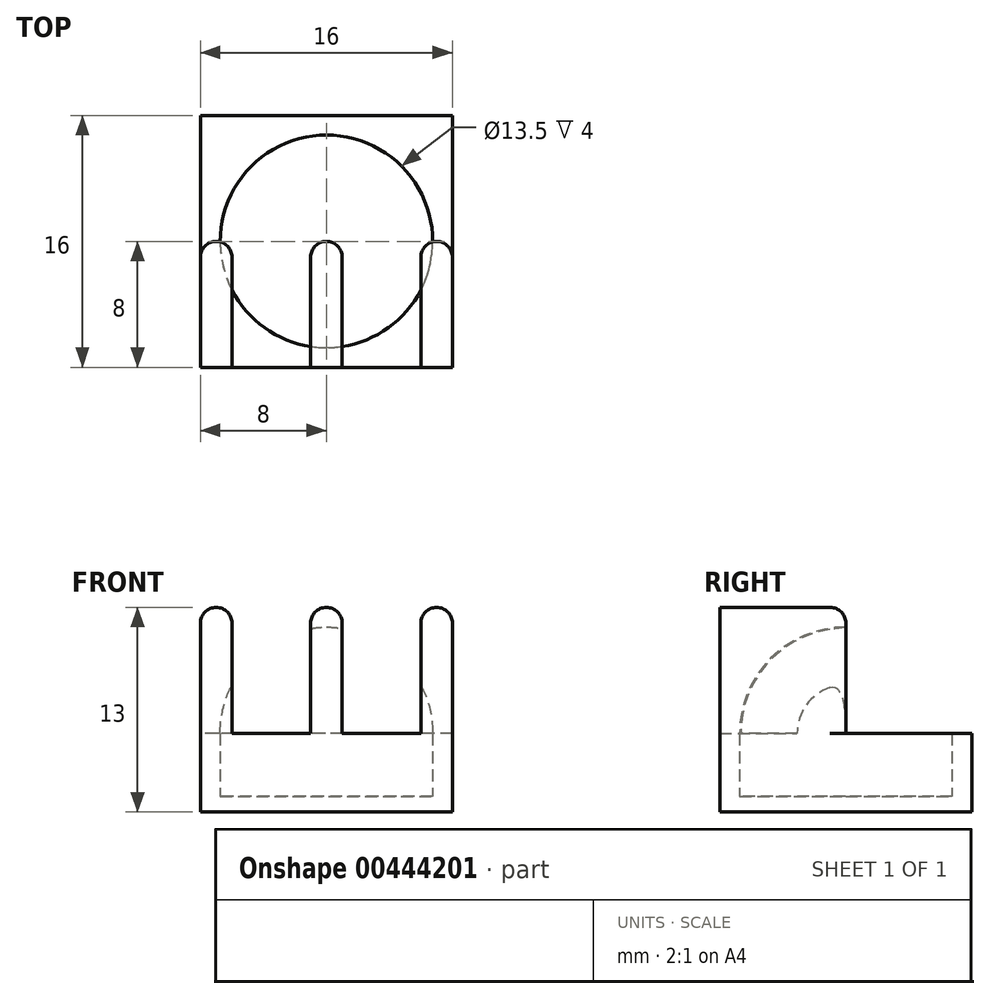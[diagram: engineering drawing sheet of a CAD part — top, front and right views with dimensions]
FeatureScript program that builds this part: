
annotation { "Feature Type Name" : "Feature", "Feature Type Description" : "" }
export const myFeature = defineFeature(function(context is Context, id is Id, definition is map)
    precondition{}
    {
        {
            var Q0;
            Q0=qCreatedBy(makeId("Top.planeOp"),FACE);
            var sketch = newSketch(context, id + "F0", { "sketchPlane" : qUnion([Q0])});
            skLineSegment(sketch, "E0.bottom", {"start": v(8, 8) * mm, "end": v(-8, 8) * mm});
            skLineSegment(sketch, "E0.top", {"start": v(8, -8) * mm, "end": v(-8, -8) * mm});
            skLineSegment(sketch, "E0.left", {"start": v(8, 8) * mm, "end": v(8, -8) * mm});
            skLineSegment(sketch, "E0.right", {"start": v(-8, 8) * mm, "end": v(-8, -8) * mm});
            skPoint(sketch, "E0.middle", {"position": v(0, 0) * mm});
            skCircle(sketch, "E1", {"center": v(0, 0) * mm, "radius": 6.75 * mm});
            skSolve(sketch);
        }
        {
            var Q0;
            Q0=makeQuery(id+"F0.imprint","IMPRINT",FACE,{"disambiguationData":[TD([[makeQuery(id+"F0.imprint","IMPRINT",EDGE,{"derivedFrom":sQuery(id+"F0.wireOp",EDGE,"E0.bottom")}),1.0]])]});
            extrude(context, id + "F1", {"entities" : qUnion([Q0]), "depth" : 5 * mm, "offsetDistance" : 25 * mm});
        }
        {
            var Q0;
            Q0=makeQuery(id+"F0.imprint","IMPRINT",FACE,{"disambiguationData":[TD([[makeQuery(id+"F0.imprint","IMPRINT",EDGE,{"derivedFrom":sQuery(id+"F0.wireOp",EDGE,"E1")}),1.0]])]});
            extrude(context, id + "F2", {"entities" : qUnion([Q0]), "operationType" : NewBodyOperationType.ADD, "depth" : 1 * mm, "offsetDistance" : 25 * mm});
        }
        {
            var Q0;
            Q0=makeQuery(id+"F1.opExtrude","CAP_FACE",FACE,{"disambiguationData":[OSD([sQuery(id+"F0.wireOp",EDGE,"E0.bottom"),sQuery(id+"F0.wireOp",EDGE,"E0.top"),sQuery(id+"F0.wireOp",EDGE,"E0.left"),sQuery(id+"F0.wireOp",EDGE,"E0.right"),sQuery(id+"F0.wireOp",EDGE,"E1")])],"isStart":false});
            var sketch = newSketch(context, id + "F3", { "sketchPlane" : qUnion([Q0])});
            skLineSegment(sketch, "E2.bottom", {"start": v(-8, -8) * mm, "end": v(-6, -8) * mm});
            skLineSegment(sketch, "E2.top", {"start": v(-8, 0) * mm, "end": v(-6, 0) * mm});
            skLineSegment(sketch, "E2.left", {"start": v(-8, -8) * mm, "end": v(-8, 0) * mm});
            skLineSegment(sketch, "E2.right", {"start": v(-6, -8) * mm, "end": v(-6, 0) * mm});
            skLineSegment(sketch, "E3.bottom", {"start": v(8, -8) * mm, "end": v(6, -8) * mm});
            skLineSegment(sketch, "E3.top", {"start": v(8, 0) * mm, "end": v(6, 0) * mm});
            skLineSegment(sketch, "E3.left", {"start": v(8, -8) * mm, "end": v(8, 0) * mm});
            skLineSegment(sketch, "E3.right", {"start": v(6, -8) * mm, "end": v(6, 0) * mm});
            skLineSegment(sketch, "E4.bottom", {"start": v(-1, -8) * mm, "end": v(1, -8) * mm});
            skLineSegment(sketch, "E4.top", {"start": v(-1, 0) * mm, "end": v(1, 0) * mm});
            skLineSegment(sketch, "E4.left", {"start": v(-1, -8) * mm, "end": v(-1, 0) * mm});
            skLineSegment(sketch, "E4.right", {"start": v(1, -8) * mm, "end": v(1, 0) * mm});
            skSolve(sketch);
        }
        {
            var Q0;
            {var subQ0=sQuery(id+"F3.wireOp",EDGE,"E2.right");var subQ1=sQuery(id+"F3.wireOp",EDGE,"E2.top");var subQ2=makeQuery(id+"F3.imprint","INTERSECT",VERTEX,{"derivedFrom":[subQ1,subQ0]});Q0=makeQuery(id+"F3.imprint","IMPRINT",FACE,{"disambiguationData":[TD([[makeQuery(id+"F3.imprint","IMPRINT",EDGE,{"disambiguationData":[TD([[subQ2,1.0]])],"derivedFrom":subQ1}),-1.0]])]});}
            var Q1;
            {var subQ1=sQuery(id+"F3.wireOp",EDGE,"E2.bottom");Q1=makeQuery(id+"F3.imprint","IMPRINT",FACE,{"disambiguationData":[TD([[makeQuery(id+"F3.imprint","IMPRINT",EDGE,{"derivedFrom":subQ1}),-1.0]])]});}
            var Q2;
            {var subQ0=sQuery(id+"F3.wireOp",EDGE,"E4.top");Q2=makeQuery(id+"F3.imprint","IMPRINT",FACE,{"disambiguationData":[TD([[makeQuery(id+"F3.imprint","IMPRINT",EDGE,{"derivedFrom":subQ0}),-1.0]])]});}
            var Q3;
            {var subQ0=sQuery(id+"F3.wireOp",EDGE,"E4.bottom");Q3=makeQuery(id+"F3.imprint","IMPRINT",FACE,{"disambiguationData":[TD([[makeQuery(id+"F3.imprint","IMPRINT",EDGE,{"derivedFrom":subQ0}),-1.0]])]});}
            var Q4;
            {var subQ1=sQuery(id+"F3.wireOp",EDGE,"E3.bottom");Q4=makeQuery(id+"F3.imprint","IMPRINT",FACE,{"disambiguationData":[TD([[makeQuery(id+"F3.imprint","IMPRINT",EDGE,{"derivedFrom":subQ1}),-1.0]])]});}
            var Q5;
            {var subQ0=sQuery(id+"F3.wireOp",EDGE,"E3.right");var subQ1=sQuery(id+"F3.wireOp",EDGE,"E3.top");var subQ2=makeQuery(id+"F3.imprint","INTERSECT",VERTEX,{"derivedFrom":[subQ1,subQ0]});Q5=makeQuery(id+"F3.imprint","IMPRINT",FACE,{"disambiguationData":[TD([[makeQuery(id+"F3.imprint","IMPRINT",EDGE,{"disambiguationData":[TD([[subQ2,1.0]])],"derivedFrom":subQ1}),1.0]])]});}
            extrude(context, id + "F4", {"entities" : qUnion([Q0, Q1, Q2, Q3, Q4, Q5]), "operationType" : NewBodyOperationType.ADD, "depth" : 8 * mm, "offsetDistance" : 25 * mm});
        }
        {
            var Q0;
            Q0=makeQuery(id+"F4.opExtrude","CAP_FACE",FACE,{"disambiguationData":[OSD([sQuery(id+"F3.wireOp",EDGE,"E4.bottom"),sQuery(id+"F3.wireOp",EDGE,"E4.top"),sQuery(id+"F3.wireOp",EDGE,"E4.left"),sQuery(id+"F3.wireOp",EDGE,"E4.right")])],"isStart":true});
            var Q1;
            Q1=makeQuery(id+"F4.opExtrude","CAP_FACE",FACE,{"disambiguationData":[OSD([sQuery(id+"F3.wireOp",EDGE,"E2.bottom"),sQuery(id+"F3.wireOp",EDGE,"E2.top"),sQuery(id+"F3.wireOp",EDGE,"E2.left"),sQuery(id+"F3.wireOp",EDGE,"E2.right")])],"isStart":true});
            var Q2;
            Q2=makeQuery(id+"F4.opExtrude","CAP_FACE",FACE,{"disambiguationData":[OSD([sQuery(id+"F3.wireOp",EDGE,"E3.bottom"),sQuery(id+"F3.wireOp",EDGE,"E3.top"),sQuery(id+"F3.wireOp",EDGE,"E3.left"),sQuery(id+"F3.wireOp",EDGE,"E3.right")])],"isStart":true});
            var Q3;
            {var subQ0=sQuery(id+"F3.wireOp",EDGE,"E2.top");var subQ1=sQuery(id+"F0.wireOp",EDGE,"E1");var subQ2=makeQuery(id+"F1.opExtrude","SWEPT_FACE",FACE,{"disambiguationData":[OSD([subQ1])]});var subQ3=makeQuery(id+"F1.opExtrude","CAP_FACE",FACE,{"disambiguationData":[OSD([sQuery(id+"F0.wireOp",EDGE,"E0.bottom"),sQuery(id+"F0.wireOp",EDGE,"E0.top"),sQuery(id+"F0.wireOp",EDGE,"E0.left"),sQuery(id+"F0.wireOp",EDGE,"E0.right"),subQ1])],"isStart":false});Q3=makeQuery(id+"F4.boolean.opBoolean","SPLIT",EDGE,{"disambiguationData":[topologyDisambiguationEdgeConnected([subQ3,subQ2]),TD([makeQuery(id+"F4.opExtrude","SWEPT_FACE",FACE,{"disambiguationData":[OSD([subQ0])]})])],"derivedFrom":makeQuery(id+"F1.opExtrude","CAP_EDGE",EDGE,{"disambiguationData":[OSD([subQ1])],"isStart":false})});}
            var Q4;
            {var subQ0=sQuery(id+"F3.wireOp",EDGE,"E3.top");Q4=makeQuery(id+"F4.boolean.opBoolean","SPLIT",EDGE,{"disambiguationData":[topologyDisambiguationEdgeConnected([makeQuery(id+"F1.opExtrude","CAP_FACE",FACE,{"disambiguationData":[OSD([sQuery(id+"F0.wireOp",EDGE,"E0.bottom"),sQuery(id+"F0.wireOp",EDGE,"E0.top"),sQuery(id+"F0.wireOp",EDGE,"E0.left"),sQuery(id+"F0.wireOp",EDGE,"E0.right"),sQuery(id+"F0.wireOp",EDGE,"E1")])],"isStart":false})])],"derivedFrom":makeQuery(id+"F4.opExtrude","CAP_EDGE",EDGE,{"disambiguationData":[OSD([subQ0])],"isStart":true})});}
            revolve(context, id + "F5", {"operationType" : NewBodyOperationType.REMOVE, "entities" : qUnion([Q0, Q1, Q2]), "surfaceEntities" : qUnion([Q3]), "axis" : qUnion([Q4]), "revolveType" : RevolveType.ONE_DIRECTION, "angle" : 90 * degree});
        }
        {
            var Q0;
            Q0=makeQuery(id+"F4.opExtrude","SWEPT_EDGE",EDGE,{"disambiguationData":[OSD([sQuery(id+"F0.wireOp",EDGE,"E0.right"),sQuery(id+"F3.wireOp",EDGE,"E2.top"),sQuery(id+"F3.wireOp",EDGE,"E2.left")])]});
            var Q1;
            Q1=makeQuery(id+"F4.opExtrude","CAP_EDGE",EDGE,{"disambiguationData":[OSD([sQuery(id+"F3.wireOp",EDGE,"E2.top")])],"isStart":false});
            var Q2;
            Q2=makeQuery(id+"F4.opExtrude","SWEPT_EDGE",EDGE,{"disambiguationData":[OSD([sQuery(id+"F3.wireOp",EDGE,"E2.top"),sQuery(id+"F3.wireOp",EDGE,"E2.right")])]});
            var Q3;
            Q3=makeQuery(id+"F4.opExtrude","CAP_EDGE",EDGE,{"disambiguationData":[OSD([sQuery(id+"F3.wireOp",EDGE,"E4.top")])],"isStart":false});
            var Q4;
            Q4=makeQuery(id+"F4.opExtrude","SWEPT_EDGE",EDGE,{"disambiguationData":[OSD([sQuery(id+"F3.wireOp",EDGE,"E4.top"),sQuery(id+"F3.wireOp",EDGE,"E4.left")])]});
            var Q5;
            Q5=makeQuery(id+"F4.opExtrude","SWEPT_EDGE",EDGE,{"disambiguationData":[OSD([sQuery(id+"F3.wireOp",EDGE,"E4.top"),sQuery(id+"F3.wireOp",EDGE,"E4.right")])]});
            var Q6;
            Q6=makeQuery(id+"F4.opExtrude","SWEPT_EDGE",EDGE,{"disambiguationData":[OSD([sQuery(id+"F0.wireOp",EDGE,"E0.left"),sQuery(id+"F3.wireOp",EDGE,"E3.top"),sQuery(id+"F3.wireOp",EDGE,"E3.left")])]});
            var Q7;
            Q7=makeQuery(id+"F4.opExtrude","SWEPT_EDGE",EDGE,{"disambiguationData":[OSD([sQuery(id+"F3.wireOp",EDGE,"E3.top"),sQuery(id+"F3.wireOp",EDGE,"E3.right")])]});
            var Q8;
            Q8=makeQuery(id+"F4.opExtrude","CAP_EDGE",EDGE,{"disambiguationData":[OSD([sQuery(id+"F3.wireOp",EDGE,"E3.top")])],"isStart":false});
            var Q9;
            Q9=makeQuery(id+"F4.opExtrude","CAP_EDGE",EDGE,{"disambiguationData":[OSD([sQuery(id+"F3.wireOp",EDGE,"E4.right")])],"isStart":false});
            var Q10;
            Q10=makeQuery(id+"F4.opExtrude","CAP_EDGE",EDGE,{"disambiguationData":[OSD([sQuery(id+"F3.wireOp",EDGE,"E4.left")])],"isStart":false});
            var Q11;
            Q11=makeQuery(id+"F4.opExtrude","CAP_EDGE",EDGE,{"disambiguationData":[OSD([sQuery(id+"F3.wireOp",EDGE,"E3.right")])],"isStart":false});
            var Q12;
            Q12=makeQuery(id+"F4.opExtrude","CAP_EDGE",EDGE,{"disambiguationData":[OSD([sQuery(id+"F3.wireOp",EDGE,"E3.left")])],"isStart":false});
            var Q13;
            Q13=makeQuery(id+"F4.opExtrude","CAP_EDGE",EDGE,{"disambiguationData":[OSD([sQuery(id+"F3.wireOp",EDGE,"E2.right")])],"isStart":false});
            var Q14;
            Q14=makeQuery(id+"F4.opExtrude","CAP_EDGE",EDGE,{"disambiguationData":[OSD([sQuery(id+"F3.wireOp",EDGE,"E2.left")])],"isStart":false});
            fillet(context, id + "F6", {"entities" : qUnion([Q0, Q1, Q2, Q3, Q4, Q5, Q6, Q7, Q8, Q9, Q10, Q11, Q12, Q13, Q14]), "radius" : 1 * mm, "tangentPropagation" : true, "allowEdgeOverflow" : false});
        }
    });
